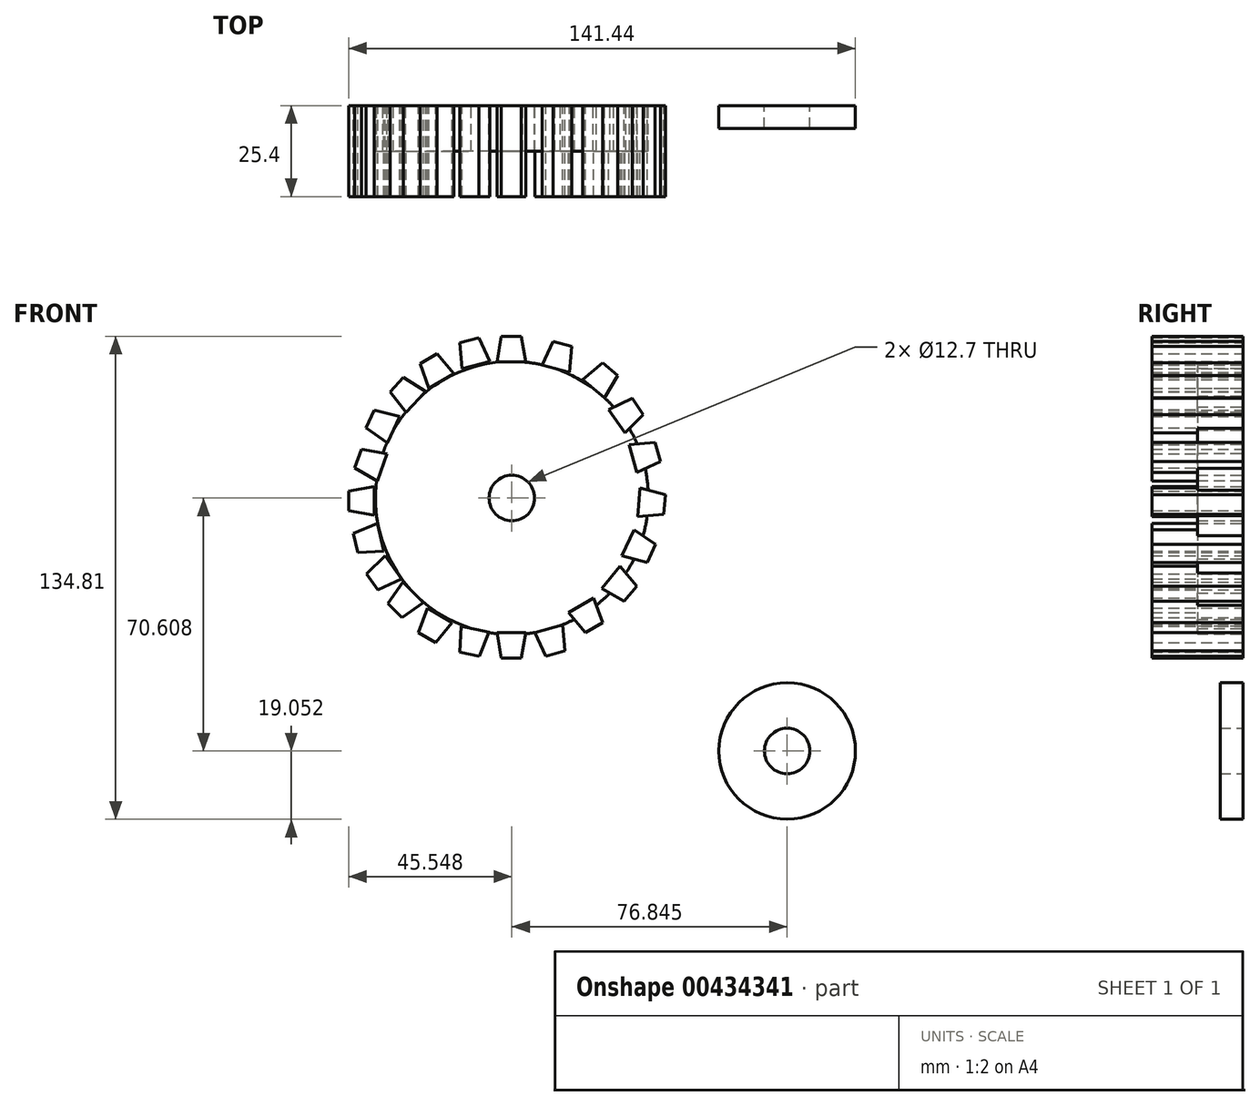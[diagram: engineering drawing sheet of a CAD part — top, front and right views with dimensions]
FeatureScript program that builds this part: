
annotation { "Feature Type Name" : "Feature", "Feature Type Description" : "" }
export const myFeature = defineFeature(function(context is Context, id is Id, definition is map)
    precondition{}
    {
        {
            var Q0;
            Q0=qCreatedBy(makeId("Front.planeOp"),FACE);
            var sketch = newSketch(context, id + "F0", { "sketchPlane" : qUnion([Q0])});
            skCircle(sketch, "E0", {"center": v(-40.74, 33) * mm, "radius": 6.35 * mm});
            skCircle(sketch, "E1", {"center": v(-40.74, 33) * mm, "radius": 38.1 * mm});
            skLineSegment(sketch, "E2", {"start": v(-78.84, 33) * mm, "end": v(-2.64, 33) * mm});
            skSolve(sketch);
        }
        {
            var Q0;
            Q0=makeQuery(id+"F0.imprint","IMPRINT",FACE,{"disambiguationData":[TD([[makeQuery(id+"F0.imprint","IMPRINT",EDGE,{"derivedFrom":sQuery(id+"F0.wireOp",EDGE,"E0")}),-1.0]])]});
            extrude(context, id + "F1", {"entities" : qUnion([Q0]), "depth" : 12.7 * mm});
        }
        {
            var Q0;
            Q0=qCreatedBy(makeId("Front.planeOp"),FACE);
            var sketch = newSketch(context, id + "F2", { "sketchPlane" : qUnion([Q0])});
            skCircle(sketch, "E3", {"center": v(36.1, -37.6) * mm, "radius": 6.35 * mm});
            skCircle(sketch, "E4", {"center": v(36.1, -37.6) * mm, "radius": 19.05 * mm});
            skSolve(sketch);
        }
        {
            var Q0;
            Q0 = qSketchRegion(id + "F2", true);
            extrude(context, id + "F3", {"entities" : qUnion([Q0]), "depth" : 6.35 * mm});
        }
        {
            var Q0;
            Q0=qCreatedBy(makeId("Front.planeOp"),FACE);
            var sketch = newSketch(context, id + "F4", { "sketchPlane" : qUnion([Q0])});
            skLineSegment(sketch, "E5", {"start": v(-43.65, 78.15) * mm, "end": v(-38.17, 78.15) * mm});
            skLineSegment(sketch, "E6", {"start": v(-38.17, 78.15) * mm, "end": v(-36.9, 70.98) * mm});
            skLineSegment(sketch, "E7", {"start": v(-36.9, 70.98) * mm, "end": v(-44.91, 70.98) * mm});
            skLineSegment(sketch, "E8", {"start": v(-44.91, 70.98) * mm, "end": v(-43.65, 78.15) * mm});
            skLineSegment(sketch, "E9", {"start": v(-29.26, 76.72) * mm, "end": v(-23.96, 75.3) * mm});
            skLineSegment(sketch, "E10", {"start": v(-23.96, 75.3) * mm, "end": v(-24.6, 68.05) * mm});
            skLineSegment(sketch, "E11", {"start": v(-24.6, 68.05) * mm, "end": v(-32.34, 70.12) * mm});
            skLineSegment(sketch, "E12", {"start": v(-32.34, 70.12) * mm, "end": v(-29.26, 76.72) * mm});
            skLineSegment(sketch, "E13", {"start": v(-15.44, 70.77) * mm, "end": v(-11.24, 67.25) * mm});
            skLineSegment(sketch, "E14", {"start": v(-11.24, 67.25) * mm, "end": v(-14.88, 60.94) * mm});
            skLineSegment(sketch, "E15", {"start": v(-14.88, 60.94) * mm, "end": v(-21.02, 66.1) * mm});
            skLineSegment(sketch, "E16", {"start": v(-21.02, 66.1) * mm, "end": v(-15.44, 70.77) * mm});
            skLineSegment(sketch, "E17", {"start": v(-7.19, 60.79) * mm, "end": v(-4.04, 56.3) * mm});
            skLineSegment(sketch, "E18", {"start": v(-4.04, 56.3) * mm, "end": v(-9.19, 51.15) * mm});
            skLineSegment(sketch, "E19", {"start": v(-9.19, 51.15) * mm, "end": v(-13.78, 57.71) * mm});
            skLineSegment(sketch, "E20", {"start": v(-13.78, 57.71) * mm, "end": v(-7.19, 60.79) * mm});
            skLineSegment(sketch, "E21", {"start": v(-0.74, 48.5) * mm, "end": v(0.68, 43.2) * mm});
            skLineSegment(sketch, "E22", {"start": v(0.68, 43.2) * mm, "end": v(-5.92, 40.12) * mm});
            skLineSegment(sketch, "E23", {"start": v(-5.92, 40.12) * mm, "end": v(-8, 47.86) * mm});
            skLineSegment(sketch, "E24", {"start": v(-8, 47.86) * mm, "end": v(-0.74, 48.5) * mm});
            skLineSegment(sketch, "E25", {"start": v(2.1, 33.92) * mm, "end": v(1.62, 28.46) * mm});
            skLineSegment(sketch, "E26", {"start": v(1.62, 28.46) * mm, "end": v(-5.64, 27.83) * mm});
            skLineSegment(sketch, "E27", {"start": v(-5.64, 27.83) * mm, "end": v(-4.94, 35.8) * mm});
            skLineSegment(sketch, "E28", {"start": v(-4.94, 35.8) * mm, "end": v(2.1, 33.92) * mm});
            skLineSegment(sketch, "E29", {"start": v(-0.65, 20.01) * mm, "end": v(-2.97, 15.04) * mm});
            skLineSegment(sketch, "E30", {"start": v(-2.97, 15.04) * mm, "end": v(-10, 16.92) * mm});
            skLineSegment(sketch, "E31", {"start": v(-10, 16.92) * mm, "end": v(-6.61, 24.19) * mm});
            skLineSegment(sketch, "E32", {"start": v(-6.61, 24.19) * mm, "end": v(-0.65, 20.01) * mm});
            skLineSegment(sketch, "E33", {"start": v(-5.84, 8.34) * mm, "end": v(-9.36, 4.14) * mm});
            skLineSegment(sketch, "E34", {"start": v(-9.36, 4.14) * mm, "end": v(-15.67, 7.78) * mm});
            skLineSegment(sketch, "E35", {"start": v(-15.67, 7.78) * mm, "end": v(-10.52, 13.92) * mm});
            skLineSegment(sketch, "E36", {"start": v(-10.52, 13.92) * mm, "end": v(-5.84, 8.34) * mm});
            skLineSegment(sketch, "E37", {"start": v(-15.44, -1.79) * mm, "end": v(-20.2, -4.53) * mm});
            skLineSegment(sketch, "E38", {"start": v(-20.2, -4.53) * mm, "end": v(-24.87, 1.05) * mm});
            skLineSegment(sketch, "E39", {"start": v(-24.87, 1.05) * mm, "end": v(-17.93, 5.06) * mm});
            skLineSegment(sketch, "E40", {"start": v(-17.93, 5.06) * mm, "end": v(-15.44, -1.79) * mm});
            skLineSegment(sketch, "E41", {"start": v(-25.93, -9.7) * mm, "end": v(-31.23, -11.11) * mm});
            skLineSegment(sketch, "E42", {"start": v(-31.23, -11.11) * mm, "end": v(-34.3, -4.52) * mm});
            skLineSegment(sketch, "E43", {"start": v(-34.3, -4.52) * mm, "end": v(-26.56, -2.44) * mm});
            skLineSegment(sketch, "E44", {"start": v(-26.56, -2.44) * mm, "end": v(-25.93, -9.7) * mm});
            skLineSegment(sketch, "E45", {"start": v(-38.17, -11.69) * mm, "end": v(-43.65, -11.69) * mm});
            skLineSegment(sketch, "E46", {"start": v(-43.65, -11.69) * mm, "end": v(-44.91, -4.52) * mm});
            skLineSegment(sketch, "E47", {"start": v(-44.91, -4.52) * mm, "end": v(-36.9, -4.52) * mm});
            skLineSegment(sketch, "E48", {"start": v(-36.9, -4.52) * mm, "end": v(-38.17, -11.69) * mm});
            skLineSegment(sketch, "E49", {"start": v(-49.85, -11.19) * mm, "end": v(-55.2, -10.03) * mm});
            skLineSegment(sketch, "E50", {"start": v(-55.2, -10.03) * mm, "end": v(-54.93, -2.76) * mm});
            skLineSegment(sketch, "E51", {"start": v(-54.93, -2.76) * mm, "end": v(-47.1, -4.45) * mm});
            skLineSegment(sketch, "E52", {"start": v(-47.1, -4.45) * mm, "end": v(-49.85, -11.19) * mm});
            skLineSegment(sketch, "E53", {"start": v(-62.05, -7.31) * mm, "end": v(-66.8, -4.57) * mm});
            skLineSegment(sketch, "E54", {"start": v(-66.8, -4.57) * mm, "end": v(-64.3, 2.27) * mm});
            skLineSegment(sketch, "E55", {"start": v(-64.3, 2.27) * mm, "end": v(-57.37, -1.74) * mm});
            skLineSegment(sketch, "E56", {"start": v(-57.37, -1.74) * mm, "end": v(-62.05, -7.31) * mm});
            skLineSegment(sketch, "E57", {"start": v(-71.44, -0.33) * mm, "end": v(-75.32, 3.55) * mm});
            skLineSegment(sketch, "E58", {"start": v(-75.32, 3.55) * mm, "end": v(-71.15, 9.51) * mm});
            skLineSegment(sketch, "E59", {"start": v(-71.15, 9.51) * mm, "end": v(-65.48, 3.85) * mm});
            skLineSegment(sketch, "E60", {"start": v(-65.48, 3.85) * mm, "end": v(-71.44, -0.33) * mm});
            skLineSegment(sketch, "E61", {"start": v(-78.1, 7.3) * mm, "end": v(-81.25, 11.8) * mm});
            skLineSegment(sketch, "E62", {"start": v(-81.25, 11.8) * mm, "end": v(-76.1, 16.95) * mm});
            skLineSegment(sketch, "E63", {"start": v(-76.1, 16.95) * mm, "end": v(-71.5, 10.39) * mm});
            skLineSegment(sketch, "E64", {"start": v(-71.5, 10.39) * mm, "end": v(-78.1, 7.3) * mm});
            skLineSegment(sketch, "E65", {"start": v(-83.73, 17.76) * mm, "end": v(-84.97, 23.1) * mm});
            skLineSegment(sketch, "E66", {"start": v(-84.97, 23.1) * mm, "end": v(-78.26, 25.95) * mm});
            skLineSegment(sketch, "E67", {"start": v(-78.26, 25.95) * mm, "end": v(-76.46, 18.14) * mm});
            skLineSegment(sketch, "E68", {"start": v(-76.46, 18.14) * mm, "end": v(-83.73, 17.76) * mm});
            skLineSegment(sketch, "E69", {"start": v(-86.29, 29.41) * mm, "end": v(-86.29, 34.9) * mm});
            skLineSegment(sketch, "E70", {"start": v(-86.29, 34.9) * mm, "end": v(-79.12, 36.16) * mm});
            skLineSegment(sketch, "E71", {"start": v(-79.12, 36.16) * mm, "end": v(-79.12, 28.15) * mm});
            skLineSegment(sketch, "E72", {"start": v(-79.12, 28.15) * mm, "end": v(-86.29, 29.41) * mm});
            skLineSegment(sketch, "E73", {"start": v(-84.6, 41.42) * mm, "end": v(-82.73, 46.57) * mm});
            skLineSegment(sketch, "E74", {"start": v(-82.73, 46.57) * mm, "end": v(-75.56, 45.3) * mm});
            skLineSegment(sketch, "E75", {"start": v(-75.56, 45.3) * mm, "end": v(-78.3, 37.78) * mm});
            skLineSegment(sketch, "E76", {"start": v(-78.3, 37.78) * mm, "end": v(-84.6, 41.42) * mm});
            skPoint(sketch, "E77", {"position": v(-79.14, 45.94) * mm});
            skLineSegment(sketch, "E78", {"start": v(-55.26, 76.33) * mm, "end": v(-49.97, 77.75) * mm});
            skLineSegment(sketch, "E79", {"start": v(-49.97, 77.75) * mm, "end": v(-46.89, 71.15) * mm});
            skLineSegment(sketch, "E80", {"start": v(-46.89, 71.15) * mm, "end": v(-54.63, 69.08) * mm});
            skLineSegment(sketch, "E81", {"start": v(-54.63, 69.08) * mm, "end": v(-55.26, 76.33) * mm});
            skLineSegment(sketch, "E82", {"start": v(-66.34, 70.52) * mm, "end": v(-61.59, 73.27) * mm});
            skLineSegment(sketch, "E83", {"start": v(-61.59, 73.27) * mm, "end": v(-56.9, 67.69) * mm});
            skLineSegment(sketch, "E84", {"start": v(-56.9, 67.69) * mm, "end": v(-63.85, 63.68) * mm});
            skLineSegment(sketch, "E85", {"start": v(-63.85, 63.68) * mm, "end": v(-66.34, 70.52) * mm});
            skLineSegment(sketch, "E86", {"start": v(-74.7, 62.6) * mm, "end": v(-71.02, 66.67) * mm});
            skLineSegment(sketch, "E87", {"start": v(-71.02, 66.67) * mm, "end": v(-64.85, 62.8) * mm});
            skLineSegment(sketch, "E88", {"start": v(-64.85, 62.8) * mm, "end": v(-70.23, 56.86) * mm});
            skLineSegment(sketch, "E89", {"start": v(-70.23, 56.86) * mm, "end": v(-74.7, 62.6) * mm});
            skLineSegment(sketch, "E90", {"start": v(-81.4, 52.62) * mm, "end": v(-79.08, 57.59) * mm});
            skLineSegment(sketch, "E91", {"start": v(-79.08, 57.59) * mm, "end": v(-72.04, 55.7) * mm});
            skLineSegment(sketch, "E92", {"start": v(-72.04, 55.7) * mm, "end": v(-75.43, 48.44) * mm});
            skLineSegment(sketch, "E93", {"start": v(-75.43, 48.44) * mm, "end": v(-81.4, 52.62) * mm});
            skSolve(sketch);
        }
        {
            var Q0;
            Q0 = qSketchRegion(id + "F4", true);
            extrude(context, id + "F5", {"entities" : qUnion([Q0]), "operationType" : NewBodyOperationType.ADD, "depth" : 25.4 * mm});
        }
    });
